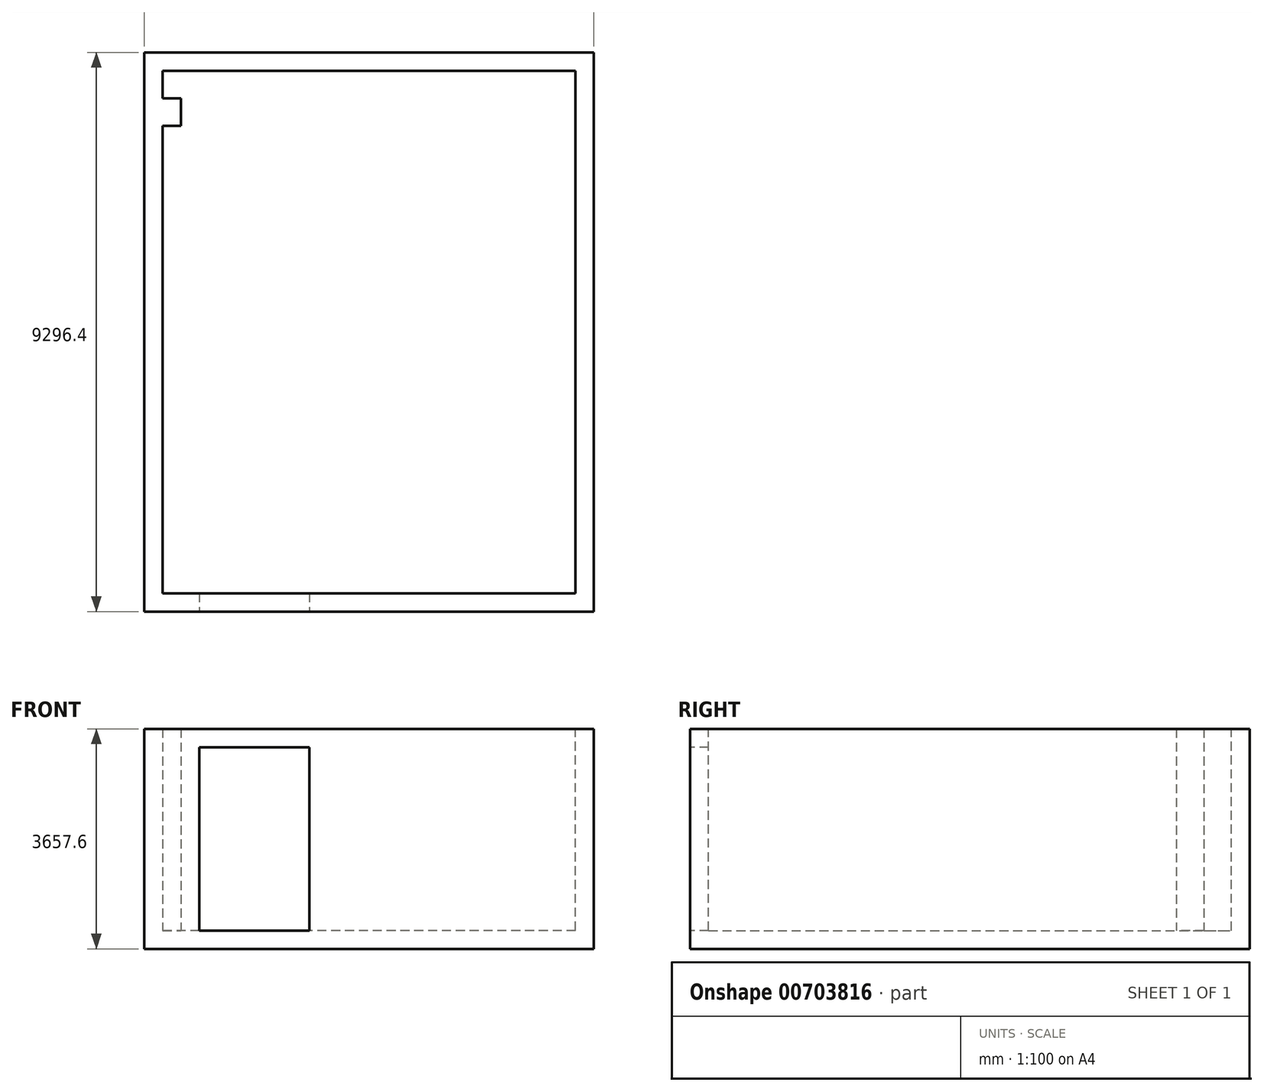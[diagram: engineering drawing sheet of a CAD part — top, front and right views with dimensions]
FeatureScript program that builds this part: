
annotation { "Feature Type Name" : "Feature", "Feature Type Description" : "" }
export const myFeature = defineFeature(function(context is Context, id is Id, definition is map)
    precondition{}
    {
        {
            var Q0;
            Q0=qCreatedBy(makeId("Top.planeOp"),FACE);
            var sketch = newSketch(context, id + "F0", { "sketchPlane" : qUnion([Q0])});
            skLineSegment(sketch, "E0.bottom", {"start": v(3733.8, -4648.2) * mm, "end": v(-3733.8, -4648.2) * mm});
            skLineSegment(sketch, "E0.top", {"start": v(3733.8, 4648.2) * mm, "end": v(-3733.8, 4648.2) * mm});
            skLineSegment(sketch, "E0.left", {"start": v(3733.8, -4648.2) * mm, "end": v(3733.8, 4648.2) * mm});
            skLineSegment(sketch, "E0.right", {"start": v(-3733.8, -4648.2) * mm, "end": v(-3733.8, 4648.2) * mm});
            skPoint(sketch, "E0.middle", {"position": v(0, 0) * mm});
            skSolve(sketch);
        }
        {
            var Q0;
            Q0 = qSketchRegion(id + "F0", true);
            extrude(context, id + "F1", {"entities" : qUnion([Q0]), "depth" : 3657.6 * mm, "offsetDistance" : 25.4 * mm});
        }
        {
            var Q0;
            Q0=makeQuery(id+"F1.opExtrude","CAP_FACE",FACE,{"disambiguationData":[OSD([sQuery(id+"F0.wireOp",EDGE,"E0.bottom"),sQuery(id+"F0.wireOp",EDGE,"E0.top"),sQuery(id+"F0.wireOp",EDGE,"E0.left"),sQuery(id+"F0.wireOp",EDGE,"E0.right")])],"isStart":false});
            var sketch = newSketch(context, id + "F2", { "sketchPlane" : qUnion([Q0])});
            skLineSegment(sketch, "E1.bottom", {"start": v(3429, -4343.4) * mm, "end": v(-3429, -4343.4) * mm});
            skLineSegment(sketch, "E1.top", {"start": v(3429, 4343.4) * mm, "end": v(-3429, 4343.4) * mm});
            skLineSegment(sketch, "E1.left", {"start": v(3429, -4343.4) * mm, "end": v(3429, 4343.4) * mm});
            skLineSegment(sketch, "E1.right", {"start": v(-3429, -4343.4) * mm, "end": v(-3429, 4343.4) * mm});
            skPoint(sketch, "E1.middle", {"position": v(0, 0) * mm});
            skSolve(sketch);
        }
        {
            var Q0;
            Q0=makeQuery(id+"F2.imprint","IMPRINT",FACE,{"disambiguationData":[TD([[makeQuery(id+"F2.imprint","IMPRINT",EDGE,{"derivedFrom":sQuery(id+"F2.wireOp",EDGE,"E1.bottom")}),-1.0]])]});
            extrude(context, id + "F3", {"entities" : qUnion([Q0]), "operationType" : NewBodyOperationType.REMOVE, "oppositeDirection" : true, "depth" : 3352.8 * mm, "offsetDistance" : 25.4 * mm});
        }
        {
            var Q0;
            Q0=makeQuery(id+"F1.opExtrude","SWEPT_FACE",FACE,{"disambiguationData":[OSD([sQuery(id+"F0.wireOp",EDGE,"E0.bottom")])]});
            var sketch = newSketch(context, id + "F4", { "sketchPlane" : qUnion([Q0])});
            skLineSegment(sketch, "E2.bottom", {"start": v(-2819.4, 304.8) * mm, "end": v(-990.6, 304.8) * mm});
            skLineSegment(sketch, "E2.top", {"start": v(-2819.4, 3352.8) * mm, "end": v(-990.6, 3352.8) * mm});
            skLineSegment(sketch, "E2.left", {"start": v(-2819.4, 304.8) * mm, "end": v(-2819.4, 3352.8) * mm});
            skLineSegment(sketch, "E2.right", {"start": v(-990.6, 304.8) * mm, "end": v(-990.6, 3352.8) * mm});
            skSolve(sketch);
        }
        {
            var Q0;
            Q0 = qSketchRegion(id + "F4", true);
            extrude(context, id + "F5", {"entities" : qUnion([Q0]), "operationType" : NewBodyOperationType.REMOVE, "endBound" : BoundingType.UP_TO_NEXT, "oppositeDirection" : true, "depth" : 25.4 * mm, "offsetDistance" : 25.4 * mm});
        }
        {
            var Q0;
            Q0=makeQuery(id+"F5.boolean.opBoolean","MERGE",FACE,{"derivedFrom":[makeQuery(id+"F3.boolean.opBoolean","COPY",FACE,{"derivedFrom":makeQuery(id+"F3.opExtrude","CAP_FACE",FACE,{"disambiguationData":[OSD([sQuery(id+"F2.wireOp",EDGE,"E1.bottom"),sQuery(id+"F2.wireOp",EDGE,"E1.top"),sQuery(id+"F2.wireOp",EDGE,"E1.left"),sQuery(id+"F2.wireOp",EDGE,"E1.right")])],"isStart":false})}),makeQuery(id+"F5.opExtrude","SWEPT_FACE",FACE,{"disambiguationData":[OSD([sQuery(id+"F4.wireOp",EDGE,"E2.bottom")])]})]});
            var sketch = newSketch(context, id + "F6", { "sketchPlane" : qUnion([Q0])});
            skLineSegment(sketch, "E3.bottom", {"start": v(-3429, 3886.2) * mm, "end": v(-3124.2, 3886.2) * mm});
            skLineSegment(sketch, "E3.top", {"start": v(-3429, 3429) * mm, "end": v(-3124.2, 3429) * mm});
            skLineSegment(sketch, "E3.left", {"start": v(-3429, 3886.2) * mm, "end": v(-3429, 3429) * mm});
            skLineSegment(sketch, "E3.right", {"start": v(-3124.2, 3886.2) * mm, "end": v(-3124.2, 3429) * mm});
            skSolve(sketch);
        }
        {
            var Q0;
            Q0 = qSketchRegion(id + "F6", true);
            var Q1;
            Q1=makeQuery(id+"F1.opExtrude","CAP_FACE",FACE,{"disambiguationData":[OSD([sQuery(id+"F0.wireOp",EDGE,"E0.bottom"),sQuery(id+"F0.wireOp",EDGE,"E0.top"),sQuery(id+"F0.wireOp",EDGE,"E0.left"),sQuery(id+"F0.wireOp",EDGE,"E0.right")])],"isStart":false});
            extrude(context, id + "F7", {"entities" : qUnion([Q0]), "operationType" : NewBodyOperationType.ADD, "endBound" : BoundingType.UP_TO_SURFACE, "depth" : 25.4 * mm, "endBoundEntityFace" : qUnion([Q1]), "offsetDistance" : 25.4 * mm});
        }
    });
